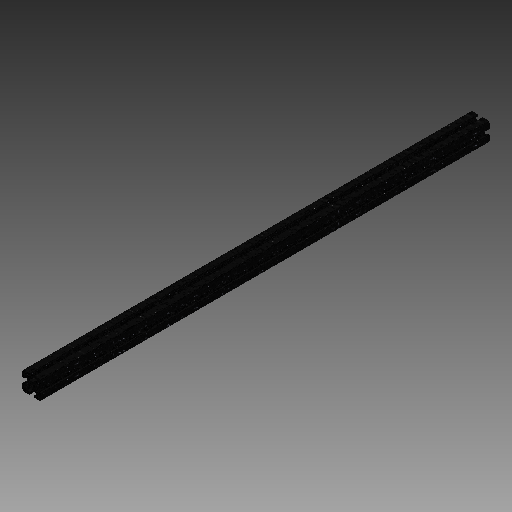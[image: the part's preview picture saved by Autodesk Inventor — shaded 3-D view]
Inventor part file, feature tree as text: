
AUTODESK INVENTOR PART (.ipt)
format: ipt  version: 2019 (Build 230136000, 136)  size: 251,904 bytes
history: native  units: in
note: dims shown in document units (in); Inventor stores cm internally (conversion verified against a paired STEP export)
features: plane x1, extrude x1, sketch x1
ambient origin geometry x8: Origin, YZ Plane, XZ Plane, XY Plane, X Axis, Y Axis, Z Axis, Center Point
bodies: Solid1 (feature_tree)
feature tree (3):
  plane  "Work Plane1"
  extrude  "Extrusion1"  [1 undecoded]
  sketch  "Sketch1"  dims[d0=36.0in d1=0.0in]
note: 1 required parameter value undecoded (feature->parameter linkage not recoverable at this tier; creation-order binding heuristic only, values carry confidence <= 0.55)
